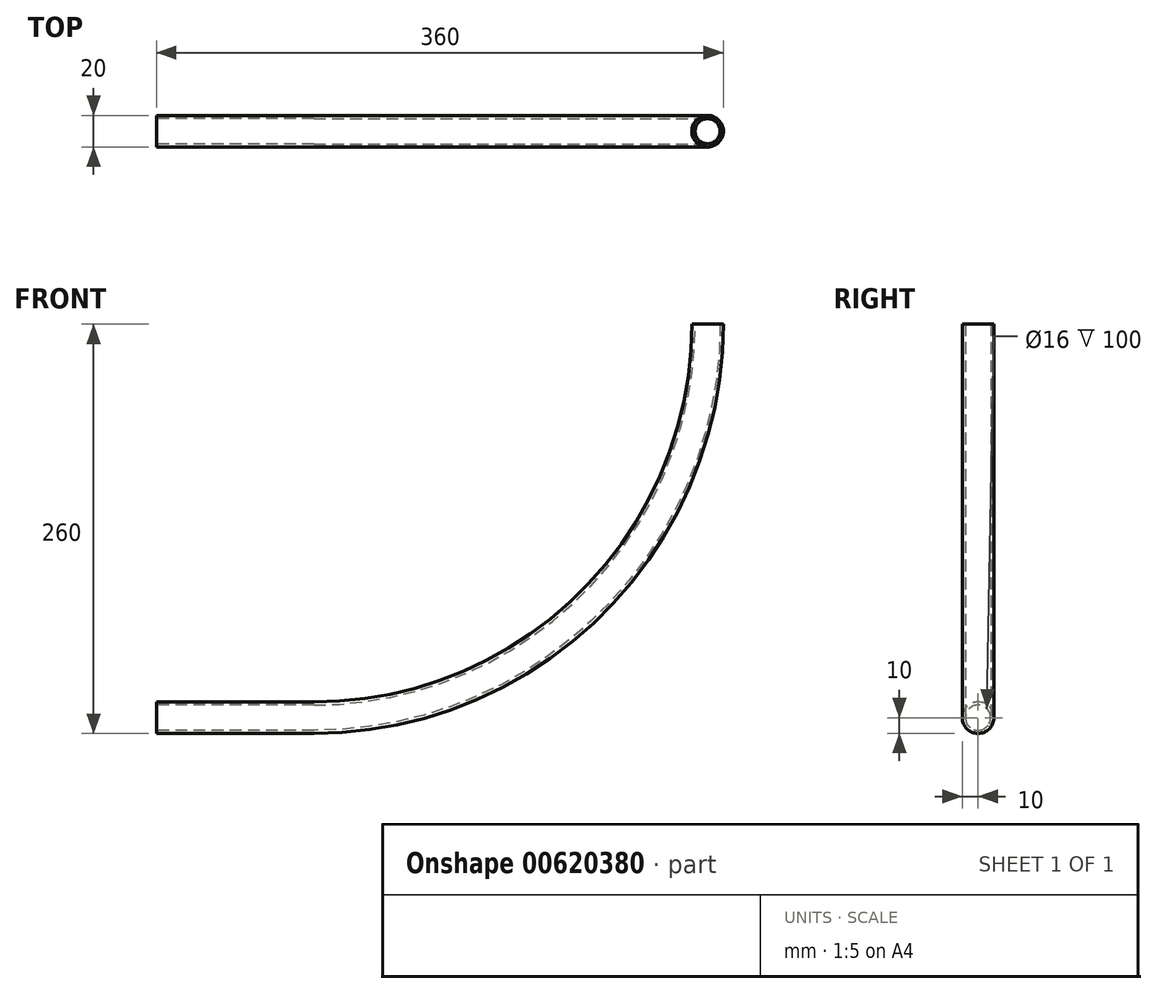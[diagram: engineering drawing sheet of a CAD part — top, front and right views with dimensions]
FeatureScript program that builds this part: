
annotation { "Feature Type Name" : "Feature", "Feature Type Description" : "" }
export const myFeature = defineFeature(function(context is Context, id is Id, definition is map)
    precondition{}
    {
        {
            var Q0;
            Q0=qCreatedBy(makeId("Front.planeOp"),FACE);
            var sketch = newSketch(context, id + "F0", { "sketchPlane" : qUnion([Q0])});
            skArc(sketch, "E0", {"start": v(0, -250) * mm, "mid": v(176.78, -176.78) * mm, "end": v(250, 0) * mm});
            skLineSegment(sketch, "E1", {"start": v(0, -250) * mm, "end": v(-100, -250) * mm});
            skSolve(sketch);
        }
        {
            var Q0;
            Q0=qCreatedBy(makeId("Right.planeOp"),FACE);
            var sketch = newSketch(context, id + "F1", { "sketchPlane" : qUnion([Q0])});
            skCircle(sketch, "E2", {"center": v(0, -250) * mm, "radius": 10 * mm});
            skCircle(sketch, "E3", {"center": v(0, -250) * mm, "radius": 8 * mm});
            skSolve(sketch);
        }
        {
            var Q0;
            Q0 = qSketchRegion(id + "F1", true);
            var Q1;
            Q1 = qConstructionFilter(qBodyType(qCreatedBy(id + "F0" ,EDGE), BodyType.WIRE), ConstructionObject.NO);
            sweep(context, id + "F2", {"profiles" : qUnion([Q0]), "path" : qUnion([Q1])});
        }
    });
